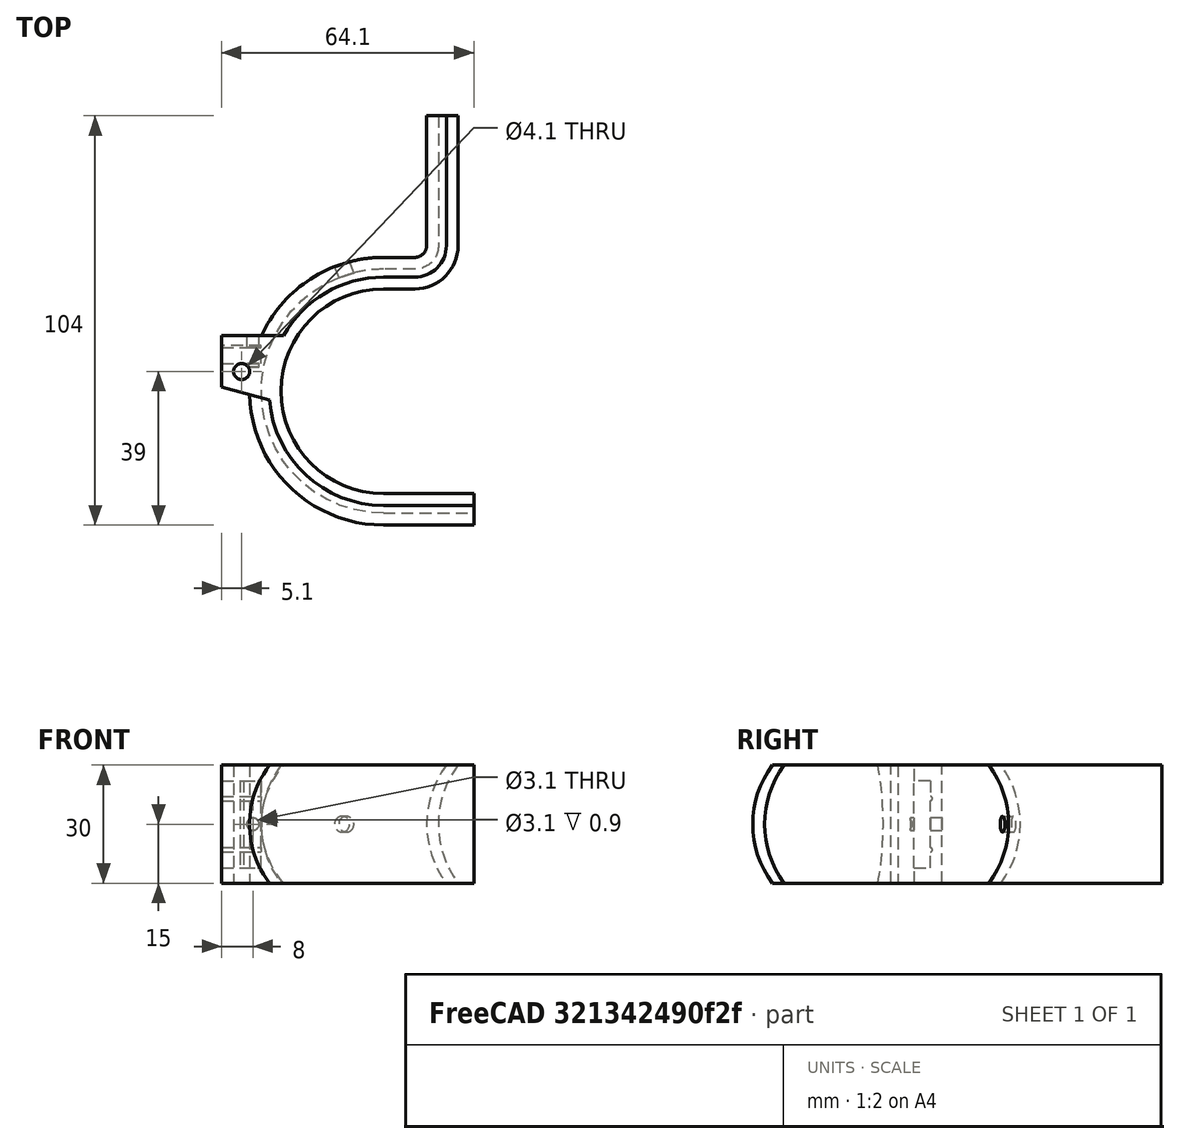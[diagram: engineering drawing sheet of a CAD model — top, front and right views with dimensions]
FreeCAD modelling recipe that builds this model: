
FCSTD DOCUMENT  (FreeCAD 0.19R)
Label: Flip
License: All rights reserved
LicenseURL: http://en.wikipedia.org/wiki/All_rights_reserved
objects: Sketcher::SketchObject×6, PartDesign::Pocket×2, PartDesign::AdditivePipe×1, PartDesign::Pad×1, PartDesign::SubtractivePipe×1, PartDesign::Body×1, Part::Cylinder×1, Part::Cut×1
note: 19 computed .brp shape members not serialized (recipe doc carries the construction recipe); baked Part::Feature solids carry a one-line shape summary decoded from their .brp

FEATURE [Sketcher::SketchObject] Sketch  label="Chemin"
  FullyConstrained = false
  MapMode = 5
  Support = -> [XY_Plane001]
  sketch-geometry (9):
    g0: LineSegment StartX=-3 StartY=95 StartZ=0 EndX=-3 EndY=62 EndZ=0
    g1: LineSegment StartX=-23 StartY=50 StartZ=0 EndX=-15 EndY=50 EndZ=0
    g2: ArcOfCircle CenterX=-15 CenterY=62 CenterZ=0 NormalX=0 NormalY=0 NormalZ=1 AngleXU=0 Radius=12 StartAngle=4.71239 EndAngle=6.28319
    g3: LineSegment StartX=-15 StartY=50 StartZ=0 EndX=-15 EndY=62 EndZ=0
    g4: LineSegment StartX=-15 StartY=62 StartZ=0 EndX=-3 EndY=62 EndZ=0
    g5: ArcOfCircle CenterX=-23 CenterY=25 CenterZ=0 NormalX=0 NormalY=0 NormalZ=1 AngleXU=0 Radius=25 StartAngle=1.5708 EndAngle=4.71239
    g6: LineSegment StartX=-23 StartY=50 StartZ=0 EndX=-23 EndY=0 EndZ=0
    g7: LineSegment StartX=-3 StartY=62 StartZ=0 EndX=-3 EndY=-0.201206 EndZ=0
    g8: LineSegment StartX=-23 StartY=0 StartZ=0 EndX=0 EndY=0 EndZ=0
  constraints (25):
    c: Vertical(g0)
    c: DistanceY(g0,g0) = 33
    c: Horizontal(g1)
    c: DistanceX(g1,g1) = 8
    c: Coincident(g2,g1)
    c: Coincident(g2,g0)
    c: Coincident(g3,g1)
    c: Vertical(g3)
    c: Coincident(g4,g3)
    c: Coincident(g4,g0)
    c: Perpendicular(g4,g3)
    c: DistanceX(g4,g4) = 12
    c: Coincident(g2,g3)
    c: Coincident(g5,g1)
    c: Coincident(g6,g1)
    c: Vertical(g6)
    c: Coincident(g5,g6)
    c: PointOnObject(g5,g6)
    c: Diameter(g5) = 50
    c: Coincident(g7,g0)
    c: Vertical(g7)
    c: Coincident(g8,g5)
    c: Horizontal(g8)
    c: Coincident(g8,g-1)
    c: DistanceX(g7,g8) = 3
FEATURE [Sketcher::SketchObject] Sketch001  label="Profil-toute-longueur"
  FullyConstrained = true
  MapMode = 5
  Placement = pos=(0,0,0) rot=(0.57735,0.57735,0.57735;2.0944rad)
  Support = -> [YZ_Plane001]
  sketch-geometry (4):
    g0: LineSegment StartX=-4 StartY=-15 StartZ=0 EndX=4 EndY=-15 EndZ=0
    g1: LineSegment StartX=4 StartY=15 StartZ=0 EndX=-4 EndY=15 EndZ=0
    g2: ArcOfCircle CenterX=16 CenterY=2.3e-15 CenterZ=0 NormalX=0 NormalY=0 NormalZ=1 AngleXU=0 Radius=25 StartAngle=2.49809 EndAngle=3.78509
    g3: LineSegment StartX=4 StartY=-15 StartZ=0 EndX=4 EndY=15 EndZ=0
  constraints (10):
    c: Symmetric(g0,g1,g-1)
    c: DistanceY(g0,g1) = 30
    c: Symmetric(g0,g1,g-1)
    c: Coincident(g2,g0)
    c: Coincident(g3,g0)
    c: Diameter(g2) = 50
    c: Symmetric(g1,g1,g-2)
    c: DistanceX(g1,g1) = 8
    c: Coincident(g1,g2)
    c: Coincident(g1,g3)
FEATURE [PartDesign::AdditivePipe] AdditivePipe  label="AdditivePipe-Flip"
  AuxilleryCurvelinear = true
  AuxillerySpineTangent = false
  Binormal = (0,0,0)
  Mode = 0
  Placement = pos=(0,0,0) rot=(0.57735,0.57735,0.57735;2.0944rad)
  Profile = -> Sketch001
  Spine = -> Sketch
  SpineTangent = false
  Transformation = 0
  Transition = 0
FEATURE [Sketcher::SketchObject] Sketch002
  ExternalGeometry = -> [AdditivePipe]
  FullyConstrained = false
  MapMode = 5
  Placement = pos=(0,-3.3e-15,-15) rot=(0.707107,0.707107,0;3.14159rad)
  Support = -> [AdditivePipe]
  sketch-geometry (6):
    g0: LineSegment StartX=26.1138 StartY=-64.1 StartZ=0 EndX=39.1 EndY=-64.1 EndZ=0
    g1: LineSegment StartX=22.7603 StartY=-51.9134 StartZ=0 EndX=26.1138 EndY=-64.1 EndZ=0
    g2: Circle CenterX=30 CenterY=-59 CenterZ=0 NormalX=0 NormalY=0 NormalZ=1 AngleXU=0 Radius=2.05
    g3: LineSegment StartX=22.7603 StartY=-51.9134 StartZ=0 EndX=39.1 EndY=-48.3415 EndZ=0
    g4: LineSegment StartX=39.1 StartY=-48.3415 StartZ=0 EndX=39.1 EndY=-64.1 EndZ=0
    g5: LineSegment StartX=25.0828 StartY=-60.3531 StartZ=0 EndX=83.1356 EndY=-44.3782 EndZ=0
  constraints (17):
    c: Horizontal(g0)
    c: Coincident(g1,g0)
    c: Diameter(g2) = 4.1
    c: Coincident(g1,g3)
    c: Coincident(g4,g0)
    c: DistanceY(g2,g-1) = 59
    c: Coincident(g4,g3)
    c: PointOnObject(g1,g-4)
    c: PointOnObject(g3,g-4)
    c: DistanceX(g-1,g2) = 30
    c: Perpendicular(g1,g5)
    c: PointOnObject(g2,g5)
    c: PointOnObject(g5,g1)
    c: Distance(g5,g2) = 5.1
    c: DistanceY(g0,g2) = 5.1
    c: DistanceX(g2,g0) = 9.1
    c: Vertical(g4)
FEATURE [PartDesign::Pad] Pad
  BaseFeature = -> AdditivePipe
  Direction = (1,1,1)
  Length = 30
  Length2 = 100
  Placement = pos=(0,0,0) rot=(0.57735,0.57735,0.57735;2.0944rad)
  Profile = -> Sketch002
  Reversed = true
  Type = 0
FEATURE [Sketcher::SketchObject] Sketch003
  FullyConstrained = true
  MapMode = 5
  Placement = pos=(0,0,0) rot=(0.57735,0.57735,0.57735;2.0944rad)
  Support = -> [Pad]
  sketch-geometry (4):
    g0: ArcOfCircle CenterX=19 CenterY=0 CenterZ=0 NormalX=0 NormalY=0 NormalZ=1 AngleXU=0 Radius=25 StartAngle=2.49809 EndAngle=3.78509
    g1: LineSegment StartX=4 StartY=15 StartZ=0 EndX=4 EndY=-15 EndZ=0
    g2: LineSegment StartX=4 StartY=15 StartZ=0 EndX=-1 EndY=15 EndZ=0
    g3: LineSegment StartX=4 StartY=-15 StartZ=0 EndX=-1 EndY=-15 EndZ=0
  constraints (12):
    c: PointOnObject(g0,g-1)
    c: Diameter(g0) = 50
    c: DistanceY(g1,g1) = 30
    c: Coincident(g2,g1)
    c: Horizontal(g2)
    c: Coincident(g3,g1)
    c: Horizontal(g3)
    c: DistanceX(g-1,g1) = 4
    c: Symmetric(g1,g1,g-1)
    c: Coincident(g0,g2)
    c: Coincident(g0,g3)
    c: DistanceX(g0,g-1) = 1
FEATURE [PartDesign::SubtractivePipe] SubtractivePipe
  AuxilleryCurvelinear = true
  AuxillerySpineTangent = false
  BaseFeature = -> Pad
  Binormal = (0,0,0)
  Mode = 0
  Placement = pos=(0,0,0) rot=(0.57735,0.57735,0.57735;2.0944rad)
  Profile = -> Sketch003
  Spine = -> Sketch
  SpineTangent = false
  Transformation = 0
  Transition = 0
FEATURE [Sketcher::SketchObject] Sketch004
  ExternalGeometry = -> [SubtractivePipe]
  FullyConstrained = true
  MapMode = 5
  Placement = pos=(-64.1,1.41e-14,-2.12e-14) rot=(0.57735,0.57735,-0.57735;4.18879rad)
  Support = -> [SubtractivePipe]
  sketch-geometry (8):
    g0: LineSegment StartX=32 StartY=11.05 StartZ=0 EndX=36.1 EndY=11.05 EndZ=0
    g1: LineSegment StartX=36.1 StartY=-11.05 StartZ=0 EndX=32 EndY=-11.05 EndZ=0
    g2: LineSegment StartX=32 StartY=11.05 StartZ=0 EndX=32 EndY=-11.05 EndZ=0
    g3: LineSegment StartX=36.1 StartY=11.05 StartZ=0 EndX=36.1 EndY=7.05 EndZ=0
    g4: LineSegment StartX=36.1 StartY=-11.05 StartZ=0 EndX=36.1 EndY=-7.05 EndZ=0
    g5: LineSegment StartX=36.1 StartY=5.95 StartZ=0 EndX=36.1 EndY=-5.95 EndZ=0
    g6: ArcOfCircle CenterX=36.1 CenterY=6.5 CenterZ=0 NormalX=0 NormalY=0 NormalZ=1 AngleXU=0 Radius=0.55 StartAngle=4.71239 EndAngle=7.85398
    g7: ArcOfCircle CenterX=36.1 CenterY=-6.5 CenterZ=0 NormalX=0 NormalY=0 NormalZ=1 AngleXU=0 Radius=0.55 StartAngle=4.71239 EndAngle=7.85398
  constraints (24):
    c: Horizontal(g0)
    c: Horizontal(g1)
    c: DistanceX(g0,g0) = 4.1
    c: DistanceY(g1,g0) = 22.1
    c: Symmetric(g1,g0,g-1)
    c: DistanceX(g0,g-3) = 3
    c: Coincident(g2,g0)
    c: Vertical(g2)
    c: Coincident(g2,g1)
    c: Coincident(g3,g0)
    c: Vertical(g3)
    c: Coincident(g4,g1)
    c: Vertical(g4)
    c: Coincident(g6,g3)
    c: Coincident(g6,g5)
    c: Coincident(g7,g5)
    c: Coincident(g7,g4)
    c: Vertical(g4,g7)
    c: Vertical(g7,g5)
    c: Vertical(g5,g5)
    c: Equal(g6,g7)
    c: Diameter(g6) = 1.1
    c: Symmetric(g7,g6,g-1)
    c: DistanceY(g7,g6) = 13
FEATURE [PartDesign::Pocket] Pocket
  BaseFeature = -> SubtractivePipe
  Length = 10
  Length2 = 100
  Placement = pos=(0,0,0) rot=(0.57735,0.57735,0.57735;2.0944rad)
  Profile = -> Sketch004
  Type = 0
FEATURE [Sketcher::SketchObject] Sketch005
  ExternalGeometry = -> [Pocket]
  FullyConstrained = true
  MapMode = 5
  Placement = pos=(1.72e-14,39.1,-1.29e-14) rot=(0.57735,0.57735,0.57735;4.18879rad)
  Support = -> [Pocket]
  sketch-geometry (1):
    g0: Circle CenterX=0 CenterY=-56.1 CenterZ=0 NormalX=0 NormalY=0 NormalZ=1 AngleXU=0 Radius=1.55
  constraints (3):
    c: PointOnObject(g0,g-2)
    c: Diameter(g0) = 3.1
    c: DistanceY(g-3,g0) = 8
FEATURE [PartDesign::Pocket] Pocket001
  BaseFeature = -> Pocket
  Length = 8
  Length2 = 100
  Placement = pos=(0,0,0) rot=(0.57735,0.57735,0.57735;2.0944rad)
  Profile = -> Sketch005
  Type = 0
FEATURE [PartDesign::Body] Body
  Group = -> [Sketch,Sketch001,AdditivePipe,Sketch002,Pad,Sketch003,SubtractivePipe,Sketch004,Pocket,Sketch005,Pocket001]
  Origin = -> Origin001
  Placement = pos=(59,-30,0) rot=(0.894305,0.447152,0.016561;0rad)
  Tip = -> Pocket001
FEATURE [Part::Cylinder] Cylinder  label="Cylindre"
  Angle = 360
  AttacherType = Attacher::AttachEngine3D
  Height = 10
  Placement = pos=(27.3202,22.5963,5e-15) rot=(0.635982,-0.437098,-0.635982;3.96574rad)
  Radius = 2
FEATURE [Part::Cut] Cut
  Base = -> Body
  Tool = -> Cylinder
